# Revit family: NLRS_57_AIR_UN_wall grill wthb supply LT_sacs
name_source: partatom
category: Air Terminals
revit_build: Autodesk Revit 2018 (Build: 20190510_1515(x64)
units: mm (PartAtom-declared; Revit-internal decimal feet)

## family parameters
Always vertical = No
Cut with Voids When Loaded = Yes
OmniClass Number = 23.75.70.21.27.11
OmniClass Title = Diffusers, Registers, and Grilles
Part Type = Normal
Room Calculation Point = Yes
Round Connector Dimension = Use Diameter
Shared = No
Work Plane-Based = No

## types (4) — shared parameters
Assembly Code = 57.0
Description = Solid Air wall diffuser WTHB (supply)
FactorTable = WTH_Factors
FireRating = 0
IfcDescription = Solid Air wall diffuser WTHB (supply)
IfcExportAs = IfcAirTerminal
IfcExportType = DIFFUSER
IsExternal = No
LoadBearing = No
LookupTable = WTHB
Manufacturer = Solid Air Climate Systems
Max Flow = 0.0 m³/h
Min Flow = 0.0 m³/h
Model = Wall diffuser
NLRS_C_content_datum_uitgifte = 27-05-2021
NLRS_C_content_provider = Solid Air Climate Solutions
NLRS_C_content_versie = 3.18.01
NLRS_C_niveau ontwikkeling = LOD 400
SACS_Material_Core = Steel
SACS_Material_Frame = Extruded Aluminium
SACS_Material_VCD = Extruded Aluminium
SACS_Show_Symbol = No
URL = https://solid-air.com

## per-type parameters (varying)
| type | SACS_Base_Index |
| WTHAO | 1 |
| WTHAV | 2 |
| WTHAB | 3 |
| WTHAS | 4 |

## geometry (parser evidence)
native form markers: Sweep x18
no freeform markers — native parametric forms only
